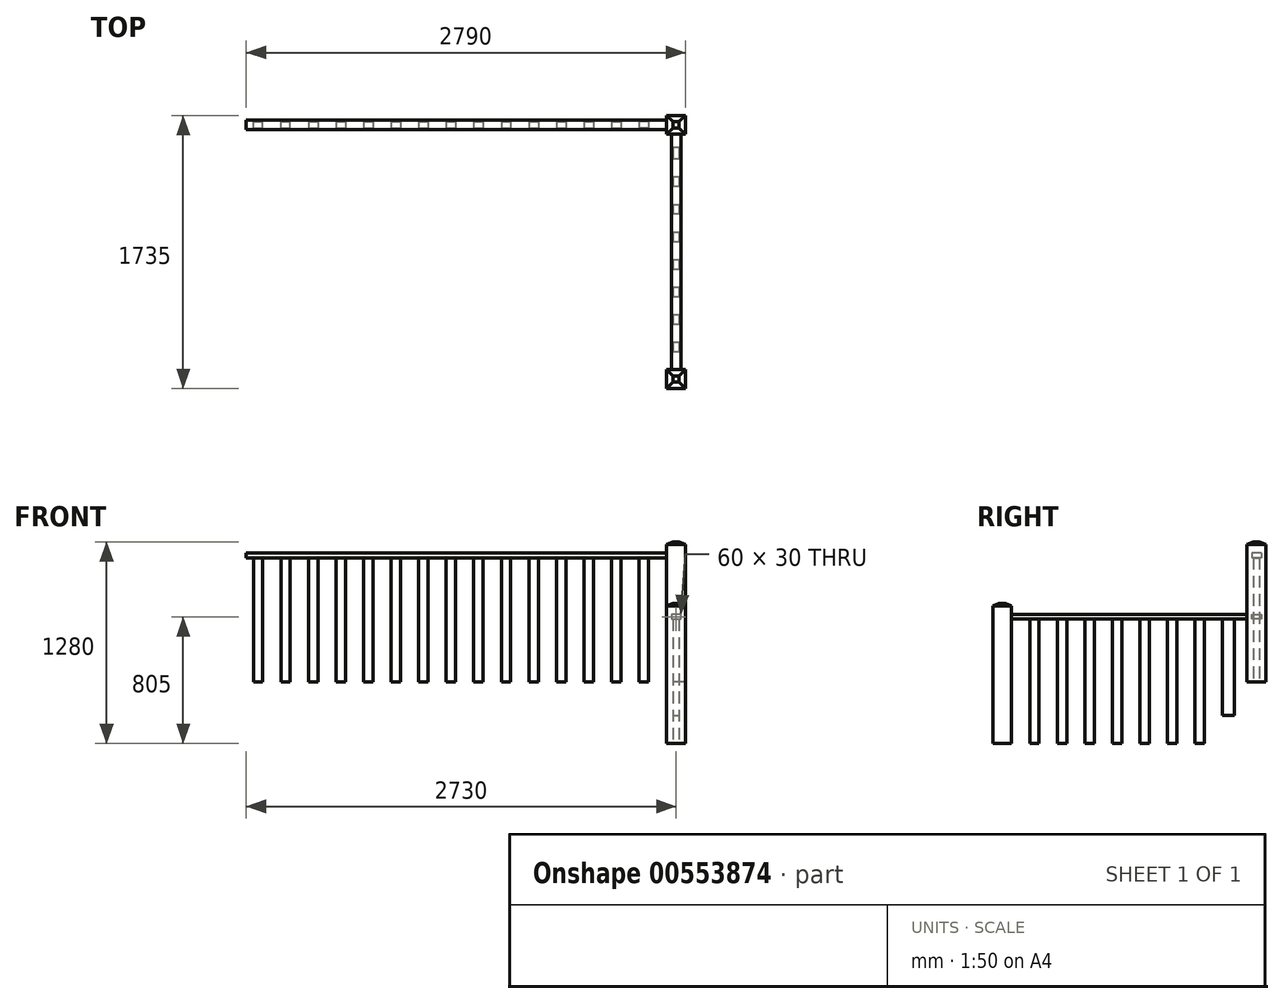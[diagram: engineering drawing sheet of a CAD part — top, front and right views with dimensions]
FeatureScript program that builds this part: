
annotation { "Feature Type Name" : "Feature", "Feature Type Description" : "" }
export const myFeature = defineFeature(function(context is Context, id is Id, definition is map)
    precondition{}
    {
        {
            var Q0;
            Q0=qCreatedBy(makeId("Top.planeOp"),FACE);
            var sketch = newSketch(context, id + "F0", { "sketchPlane" : qUnion([Q0])});
            skLineSegment(sketch, "E0.bottom", {"start": v(-80, 328.24) * mm, "end": v(40, 328.24) * mm});
            skLineSegment(sketch, "E0.top", {"start": v(-80, 208.24) * mm, "end": v(40, 208.24) * mm});
            skLineSegment(sketch, "E0.left", {"start": v(-80, 328.24) * mm, "end": v(-80, 208.24) * mm});
            skLineSegment(sketch, "E0.right", {"start": v(40, 328.24) * mm, "end": v(40, 208.24) * mm});
            skLineSegment(sketch, "E1.top", {"start": v(-80, 1823.24) * mm, "end": v(40, 1823.24) * mm});
            skLineSegment(sketch, "E1.left", {"start": v(-80, 1943.24) * mm, "end": v(-80, 1823.24) * mm});
            skLineSegment(sketch, "E1.right", {"start": v(40, 1943.24) * mm, "end": v(40, 1823.24) * mm});
            skLineSegment(sketch, "E2.bottom", {"start": v(-40, 503.24) * mm, "end": v(0, 503.24) * mm});
            skLineSegment(sketch, "E2.top", {"start": v(-40, 443.24) * mm, "end": v(0, 443.24) * mm});
            skLineSegment(sketch, "E2.left", {"start": v(-40, 503.24) * mm, "end": v(-40, 443.24) * mm});
            skLineSegment(sketch, "E2.right", {"start": v(0, 503.24) * mm, "end": v(0, 443.24) * mm});
            skLineSegment(sketch, "E3.bottom", {"start": v(-40, 678.24) * mm, "end": v(0, 678.24) * mm});
            skLineSegment(sketch, "E3.top", {"start": v(-40, 618.24) * mm, "end": v(0, 618.24) * mm});
            skLineSegment(sketch, "E3.left", {"start": v(-40, 678.24) * mm, "end": v(-40, 618.24) * mm});
            skLineSegment(sketch, "E3.right", {"start": v(0, 678.24) * mm, "end": v(0, 618.24) * mm});
            skLineSegment(sketch, "E4.bottom", {"start": v(-40, 853.24) * mm, "end": v(0, 853.24) * mm});
            skLineSegment(sketch, "E4.top", {"start": v(-40, 793.24) * mm, "end": v(0, 793.24) * mm});
            skLineSegment(sketch, "E4.left", {"start": v(-40, 853.24) * mm, "end": v(-40, 793.24) * mm});
            skLineSegment(sketch, "E4.right", {"start": v(0, 853.24) * mm, "end": v(0, 793.24) * mm});
            skLineSegment(sketch, "E5.bottom", {"start": v(-40, 1028.24) * mm, "end": v(0, 1028.24) * mm});
            skLineSegment(sketch, "E5.top", {"start": v(-40, 968.24) * mm, "end": v(0, 968.24) * mm});
            skLineSegment(sketch, "E5.left", {"start": v(-40, 1028.24) * mm, "end": v(-40, 968.24) * mm});
            skLineSegment(sketch, "E5.right", {"start": v(0, 1028.24) * mm, "end": v(0, 968.24) * mm});
            skLineSegment(sketch, "E6.bottom", {"start": v(-40, 1203.24) * mm, "end": v(0, 1203.24) * mm});
            skLineSegment(sketch, "E6.top", {"start": v(-40, 1143.24) * mm, "end": v(0, 1143.24) * mm});
            skLineSegment(sketch, "E6.left", {"start": v(-40, 1203.24) * mm, "end": v(-40, 1143.24) * mm});
            skLineSegment(sketch, "E6.right", {"start": v(0, 1203.24) * mm, "end": v(0, 1143.24) * mm});
            skLineSegment(sketch, "E7.bottom", {"start": v(-40, 1378.24) * mm, "end": v(0, 1378.24) * mm});
            skLineSegment(sketch, "E7.top", {"start": v(-40, 1318.24) * mm, "end": v(0, 1318.24) * mm});
            skLineSegment(sketch, "E7.left", {"start": v(-40, 1378.24) * mm, "end": v(-40, 1318.24) * mm});
            skLineSegment(sketch, "E7.right", {"start": v(0, 1378.24) * mm, "end": v(0, 1318.24) * mm});
            skLineSegment(sketch, "E8.bottom", {"start": v(-40, 1553.24) * mm, "end": v(0, 1553.24) * mm});
            skLineSegment(sketch, "E8.top", {"start": v(-40, 1493.24) * mm, "end": v(0, 1493.24) * mm});
            skLineSegment(sketch, "E8.left", {"start": v(-40, 1553.24) * mm, "end": v(-40, 1493.24) * mm});
            skLineSegment(sketch, "E8.right", {"start": v(0, 1553.24) * mm, "end": v(0, 1478.21) * mm});
            skLineSegment(sketch, "E9.bottom", {"start": v(-40, 1743.26) * mm, "end": v(0, 1743.26) * mm});
            skLineSegment(sketch, "E9.top", {"start": v(-40, 1668.24) * mm, "end": v(0, 1668.24) * mm});
            skLineSegment(sketch, "E9.left", {"start": v(-40, 1743.26) * mm, "end": v(-40, 1668.24) * mm});
            skLineSegment(sketch, "E9.right", {"start": v(0, 1743.26) * mm, "end": v(0, 1668.24) * mm});
            skLineSegment(sketch, "E10", {"start": v(40, 1943.24) * mm, "end": v(-80, 1943.24) * mm});
            skLineSegment(sketch, "E11.bottom", {"start": v(-195, 1903.24) * mm, "end": v(-255, 1903.24) * mm});
            skLineSegment(sketch, "E11.top", {"start": v(-195, 1863.24) * mm, "end": v(-255, 1863.24) * mm});
            skLineSegment(sketch, "E11.left", {"start": v(-195, 1903.24) * mm, "end": v(-195, 1863.24) * mm});
            skLineSegment(sketch, "E11.right", {"start": v(-255, 1903.24) * mm, "end": v(-255, 1863.24) * mm});
            skLineSegment(sketch, "E12.bottom", {"start": v(-370, 1903.24) * mm, "end": v(-430, 1903.24) * mm});
            skLineSegment(sketch, "E12.top", {"start": v(-370, 1863.24) * mm, "end": v(-430, 1863.24) * mm});
            skLineSegment(sketch, "E12.left", {"start": v(-370, 1903.24) * mm, "end": v(-370, 1863.24) * mm});
            skLineSegment(sketch, "E12.right", {"start": v(-430, 1903.24) * mm, "end": v(-430, 1863.24) * mm});
            skLineSegment(sketch, "E13.bottom", {"start": v(-545, 1903.24) * mm, "end": v(-605, 1903.24) * mm});
            skLineSegment(sketch, "E13.top", {"start": v(-545, 1863.24) * mm, "end": v(-605, 1863.24) * mm});
            skLineSegment(sketch, "E13.left", {"start": v(-545, 1903.24) * mm, "end": v(-545, 1863.24) * mm});
            skLineSegment(sketch, "E13.right", {"start": v(-605, 1903.24) * mm, "end": v(-605, 1863.24) * mm});
            skLineSegment(sketch, "E14.bottom", {"start": v(-720, 1903.24) * mm, "end": v(-780, 1903.24) * mm});
            skLineSegment(sketch, "E14.top", {"start": v(-720, 1863.24) * mm, "end": v(-780, 1863.24) * mm});
            skLineSegment(sketch, "E14.left", {"start": v(-720, 1903.24) * mm, "end": v(-720, 1863.24) * mm});
            skLineSegment(sketch, "E14.right", {"start": v(-780, 1903.24) * mm, "end": v(-780, 1863.24) * mm});
            skLineSegment(sketch, "E15.bottom", {"start": v(-895, 1903.24) * mm, "end": v(-955, 1903.24) * mm});
            skLineSegment(sketch, "E15.top", {"start": v(-895, 1863.24) * mm, "end": v(-955, 1863.24) * mm});
            skLineSegment(sketch, "E15.left", {"start": v(-895, 1903.24) * mm, "end": v(-895, 1863.24) * mm});
            skLineSegment(sketch, "E15.right", {"start": v(-955, 1903.24) * mm, "end": v(-955, 1863.24) * mm});
            skLineSegment(sketch, "E16.bottom", {"start": v(-1070, 1903.24) * mm, "end": v(-1130, 1903.24) * mm});
            skLineSegment(sketch, "E16.top", {"start": v(-1070, 1863.24) * mm, "end": v(-1130, 1863.24) * mm});
            skLineSegment(sketch, "E16.left", {"start": v(-1070, 1903.24) * mm, "end": v(-1070, 1863.24) * mm});
            skLineSegment(sketch, "E16.right", {"start": v(-1130, 1903.24) * mm, "end": v(-1130, 1863.24) * mm});
            skLineSegment(sketch, "E17.bottom", {"start": v(-1245, 1903.24) * mm, "end": v(-1305, 1903.24) * mm});
            skLineSegment(sketch, "E17.top", {"start": v(-1245, 1863.24) * mm, "end": v(-1305, 1863.24) * mm});
            skLineSegment(sketch, "E17.left", {"start": v(-1245, 1903.24) * mm, "end": v(-1245, 1863.24) * mm});
            skLineSegment(sketch, "E17.right", {"start": v(-1305, 1903.24) * mm, "end": v(-1305, 1863.24) * mm});
            skLineSegment(sketch, "E18.bottom", {"start": v(-1420, 1903.24) * mm, "end": v(-1480, 1903.24) * mm});
            skLineSegment(sketch, "E18.top", {"start": v(-1420, 1863.24) * mm, "end": v(-1480, 1863.24) * mm});
            skLineSegment(sketch, "E18.left", {"start": v(-1420, 1903.24) * mm, "end": v(-1420, 1863.24) * mm});
            skLineSegment(sketch, "E18.right", {"start": v(-1480, 1903.24) * mm, "end": v(-1480, 1863.24) * mm});
            skLineSegment(sketch, "E19.bottom", {"start": v(-1655, 1903.24) * mm, "end": v(-1595, 1903.24) * mm});
            skLineSegment(sketch, "E19.top", {"start": v(-1655, 1863.24) * mm, "end": v(-1595, 1863.24) * mm});
            skLineSegment(sketch, "E19.left", {"start": v(-1655, 1903.24) * mm, "end": v(-1655, 1863.24) * mm});
            skLineSegment(sketch, "E19.right", {"start": v(-1595, 1903.24) * mm, "end": v(-1595, 1863.24) * mm});
            skLineSegment(sketch, "E20.bottom", {"start": v(-1830, 1903.24) * mm, "end": v(-1770, 1903.24) * mm});
            skLineSegment(sketch, "E20.top", {"start": v(-1830, 1863.24) * mm, "end": v(-1770, 1863.24) * mm});
            skLineSegment(sketch, "E20.left", {"start": v(-1830, 1903.24) * mm, "end": v(-1830, 1863.24) * mm});
            skLineSegment(sketch, "E20.right", {"start": v(-1770, 1903.24) * mm, "end": v(-1770, 1863.24) * mm});
            skLineSegment(sketch, "E21.bottom", {"start": v(-2005, 1903.24) * mm, "end": v(-1945, 1903.24) * mm});
            skLineSegment(sketch, "E21.top", {"start": v(-2005, 1863.24) * mm, "end": v(-1945, 1863.24) * mm});
            skLineSegment(sketch, "E21.left", {"start": v(-2005, 1903.24) * mm, "end": v(-2005, 1863.24) * mm});
            skLineSegment(sketch, "E21.right", {"start": v(-1945, 1903.24) * mm, "end": v(-1945, 1863.24) * mm});
            skLineSegment(sketch, "E22.bottom", {"start": v(-2180, 1903.24) * mm, "end": v(-2120, 1903.24) * mm});
            skLineSegment(sketch, "E22.top", {"start": v(-2180, 1863.24) * mm, "end": v(-2120, 1863.24) * mm});
            skLineSegment(sketch, "E22.left", {"start": v(-2180, 1903.24) * mm, "end": v(-2180, 1863.24) * mm});
            skLineSegment(sketch, "E22.right", {"start": v(-2120, 1903.24) * mm, "end": v(-2120, 1863.24) * mm});
            skLineSegment(sketch, "E23.bottom", {"start": v(-2355, 1903.24) * mm, "end": v(-2295, 1903.24) * mm});
            skLineSegment(sketch, "E23.top", {"start": v(-2355, 1863.24) * mm, "end": v(-2295, 1863.24) * mm});
            skLineSegment(sketch, "E23.left", {"start": v(-2355, 1903.24) * mm, "end": v(-2355, 1863.24) * mm});
            skLineSegment(sketch, "E23.right", {"start": v(-2295, 1903.24) * mm, "end": v(-2295, 1863.24) * mm});
            skSolve(sketch);
        }
        {
            var Q0;
            Q0=makeQuery(id+"F0.imprint","IMPRINT",FACE,{"disambiguationData":[TD([[makeQuery(id+"F0.imprint","IMPRINT",EDGE,{"derivedFrom":sQuery(id+"F0.wireOp",EDGE,"E23.bottom")}),-1.0]])]});
            var Q1;
            Q1=makeQuery(id+"F0.imprint","IMPRINT",FACE,{"disambiguationData":[TD([[makeQuery(id+"F0.imprint","IMPRINT",EDGE,{"derivedFrom":sQuery(id+"F0.wireOp",EDGE,"E22.bottom")}),-1.0]])]});
            var Q2;
            Q2=makeQuery(id+"F0.imprint","IMPRINT",FACE,{"disambiguationData":[TD([[makeQuery(id+"F0.imprint","IMPRINT",EDGE,{"derivedFrom":sQuery(id+"F0.wireOp",EDGE,"E21.bottom")}),-1.0]])]});
            var Q3;
            Q3=makeQuery(id+"F0.imprint","IMPRINT",FACE,{"disambiguationData":[TD([[makeQuery(id+"F0.imprint","IMPRINT",EDGE,{"derivedFrom":sQuery(id+"F0.wireOp",EDGE,"E20.bottom")}),-1.0]])]});
            var Q4;
            Q4=makeQuery(id+"F0.imprint","IMPRINT",FACE,{"disambiguationData":[TD([[makeQuery(id+"F0.imprint","IMPRINT",EDGE,{"derivedFrom":sQuery(id+"F0.wireOp",EDGE,"E19.bottom")}),-1.0]])]});
            var Q5;
            Q5=makeQuery(id+"F0.imprint","IMPRINT",FACE,{"disambiguationData":[TD([[makeQuery(id+"F0.imprint","IMPRINT",EDGE,{"derivedFrom":sQuery(id+"F0.wireOp",EDGE,"E18.bottom")}),1.0]])]});
            var Q6;
            Q6=makeQuery(id+"F0.imprint","IMPRINT",FACE,{"disambiguationData":[TD([[makeQuery(id+"F0.imprint","IMPRINT",EDGE,{"derivedFrom":sQuery(id+"F0.wireOp",EDGE,"E17.bottom")}),1.0]])]});
            var Q7;
            Q7=makeQuery(id+"F0.imprint","IMPRINT",FACE,{"disambiguationData":[TD([[makeQuery(id+"F0.imprint","IMPRINT",EDGE,{"derivedFrom":sQuery(id+"F0.wireOp",EDGE,"E16.bottom")}),1.0]])]});
            var Q8;
            Q8=makeQuery(id+"F0.imprint","IMPRINT",FACE,{"disambiguationData":[TD([[makeQuery(id+"F0.imprint","IMPRINT",EDGE,{"derivedFrom":sQuery(id+"F0.wireOp",EDGE,"E15.bottom")}),1.0]])]});
            var Q9;
            Q9=makeQuery(id+"F0.imprint","IMPRINT",FACE,{"disambiguationData":[TD([[makeQuery(id+"F0.imprint","IMPRINT",EDGE,{"derivedFrom":sQuery(id+"F0.wireOp",EDGE,"E14.bottom")}),1.0]])]});
            var Q10;
            Q10=makeQuery(id+"F0.imprint","IMPRINT",FACE,{"disambiguationData":[TD([[makeQuery(id+"F0.imprint","IMPRINT",EDGE,{"derivedFrom":sQuery(id+"F0.wireOp",EDGE,"E13.bottom")}),1.0]])]});
            var Q11;
            Q11=makeQuery(id+"F0.imprint","IMPRINT",FACE,{"disambiguationData":[TD([[makeQuery(id+"F0.imprint","IMPRINT",EDGE,{"derivedFrom":sQuery(id+"F0.wireOp",EDGE,"E12.bottom")}),1.0]])]});
            var Q12;
            Q12=makeQuery(id+"F0.imprint","IMPRINT",FACE,{"disambiguationData":[TD([[makeQuery(id+"F0.imprint","IMPRINT",EDGE,{"derivedFrom":sQuery(id+"F0.wireOp",EDGE,"E11.bottom")}),1.0]])]});
            var Q13;
            Q13=makeQuery(id+"F0.imprint","IMPRINT",FACE,{"disambiguationData":[TD([[makeQuery(id+"F0.imprint","IMPRINT",EDGE,{"derivedFrom":sQuery(id+"F0.wireOp",EDGE,"E9.bottom")}),-1.0]])]});
            var Q14;
            {var subQ0=sQuery(id+"F0.wireOp",EDGE,"E8.bottom");Q14=makeQuery(id+"F0.imprint","IMPRINT",FACE,{"disambiguationData":[TD([[makeQuery(id+"F0.imprint","IMPRINT",EDGE,{"derivedFrom":subQ0}),-1.0]])]});}
            var Q15;
            Q15=makeQuery(id+"F0.imprint","IMPRINT",FACE,{"disambiguationData":[TD([[makeQuery(id+"F0.imprint","IMPRINT",EDGE,{"derivedFrom":sQuery(id+"F0.wireOp",EDGE,"E7.bottom")}),-1.0]])]});
            var Q16;
            Q16=makeQuery(id+"F0.imprint","IMPRINT",FACE,{"disambiguationData":[TD([[makeQuery(id+"F0.imprint","IMPRINT",EDGE,{"derivedFrom":sQuery(id+"F0.wireOp",EDGE,"E6.bottom")}),-1.0]])]});
            var Q17;
            Q17=makeQuery(id+"F0.imprint","IMPRINT",FACE,{"disambiguationData":[TD([[makeQuery(id+"F0.imprint","IMPRINT",EDGE,{"derivedFrom":sQuery(id+"F0.wireOp",EDGE,"E5.bottom")}),-1.0]])]});
            var Q18;
            Q18=makeQuery(id+"F0.imprint","IMPRINT",FACE,{"disambiguationData":[TD([[makeQuery(id+"F0.imprint","IMPRINT",EDGE,{"derivedFrom":sQuery(id+"F0.wireOp",EDGE,"E4.bottom")}),-1.0]])]});
            var Q19;
            Q19=makeQuery(id+"F0.imprint","IMPRINT",FACE,{"disambiguationData":[TD([[makeQuery(id+"F0.imprint","IMPRINT",EDGE,{"derivedFrom":sQuery(id+"F0.wireOp",EDGE,"E3.bottom")}),-1.0]])]});
            var Q20;
            Q20=makeQuery(id+"F0.imprint","IMPRINT",FACE,{"disambiguationData":[TD([[makeQuery(id+"F0.imprint","IMPRINT",EDGE,{"derivedFrom":sQuery(id+"F0.wireOp",EDGE,"E2.bottom")}),-1.0]])]});
            var Q21;
            Q21=makeQuery(id+"F0.imprint","IMPRINT",FACE,{"disambiguationData":[TD([[makeQuery(id+"F0.imprint","IMPRINT",EDGE,{"derivedFrom":sQuery(id+"F0.wireOp",EDGE,"E1.top")}),1.0]])]});
            var Q22;
            Q22=makeQuery(id+"F0.imprint","IMPRINT",FACE,{"disambiguationData":[TD([[makeQuery(id+"F0.imprint","IMPRINT",EDGE,{"derivedFrom":sQuery(id+"F0.wireOp",EDGE,"E0.bottom")}),-1.0]])]});
            extrude(context, id + "F1", {"entities" : qUnion([Q0, Q1, Q2, Q3, Q4, Q5, Q6, Q7, Q8, Q9, Q10, Q11, Q12, Q13, Q14, Q15, Q16, Q17, Q18, Q19, Q20, Q21, Q22]), "depth" : 790 * mm});
        }
        {
            var Q0;
            Q0=makeQuery(id+"F1.opExtrude","CAP_FACE",FACE,{"disambiguationData":[OSD([sQuery(id+"F0.wireOp",EDGE,"E9.bottom"),sQuery(id+"F0.wireOp",EDGE,"E9.top"),sQuery(id+"F0.wireOp",EDGE,"E9.left"),sQuery(id+"F0.wireOp",EDGE,"E9.right")])],"isStart":false});
            var sketch = newSketch(context, id + "F2", { "sketchPlane" : qUnion([Q0])});
            skPoint(sketch, "E24.0", {"position": v(-20, 328.24) * mm});
            skLineSegment(sketch, "E25.0", {"start": v(-80, 328.24) * mm, "end": v(40, 328.24) * mm});
            skLineSegment(sketch, "E26.0.0", {"start": v(-80, 328.24) * mm, "end": v(-80, 208.24) * mm});
            skLineSegment(sketch, "E26.0.1", {"start": v(-80, 208.24) * mm, "end": v(40, 208.24) * mm});
            skLineSegment(sketch, "E26.0.2", {"start": v(40, 208.24) * mm, "end": v(40, 328.24) * mm});
            skLineSegment(sketch, "E26.0.3", {"start": v(40, 328.24) * mm, "end": v(-80, 328.24) * mm});
            skLineSegment(sketch, "E27", {"start": v(-50, 1853.24) * mm, "end": v(-2417.72, 1853.24) * mm});
            skLineSegment(sketch, "E28", {"start": v(-2417.72, 1853.24) * mm, "end": v(-2417.72, 1913.24) * mm});
            skLineSegment(sketch, "E29", {"start": v(-2417.72, 1913.24) * mm, "end": v(10, 1913.24) * mm});
            skLineSegment(sketch, "E30", {"start": v(10, 1913.24) * mm, "end": v(10, 328.24) * mm});
            skLineSegment(sketch, "E31", {"start": v(10, 328.24) * mm, "end": v(-50, 328.24) * mm});
            skLineSegment(sketch, "E32", {"start": v(-50, 328.24) * mm, "end": v(-50, 1853.24) * mm});
            skSolve(sketch);
        }
        {
            var Q0;
            Q0=qSketchRegion(id+"F2",true);
            extrude(context, id + "F3", {"entities" : qUnion([Q0]), "depth" : 30 * mm});
        }
        {
            var Q0;
            Q0=makeQuery(id+"F1.opExtrude","CAP_FACE",FACE,{"disambiguationData":[OSD([sQuery(id+"F0.wireOp",EDGE,"E1.top"),sQuery(id+"F0.wireOp",EDGE,"E1.left"),sQuery(id+"F0.wireOp",EDGE,"E1.right"),sQuery(id+"F0.wireOp",EDGE,"E10")])],"isStart":false});
            var sketch = newSketch(context, id + "F4", { "sketchPlane" : qUnion([Q0])});
            skLineSegment(sketch, "E33.0", {"start": v(40, 1943.24) * mm, "end": v(-80, 1943.24) * mm});
            skLineSegment(sketch, "E34.0", {"start": v(-80, 1943.24) * mm, "end": v(-80, 1823.24) * mm});
            skLineSegment(sketch, "E35.0", {"start": v(-80, 1823.24) * mm, "end": v(40, 1823.24) * mm});
            skLineSegment(sketch, "E36.0", {"start": v(40, 1943.24) * mm, "end": v(40, 1823.24) * mm});
            skLineSegment(sketch, "E37.0", {"start": v(-80, 328.24) * mm, "end": v(-80, 208.24) * mm});
            skPoint(sketch, "E38.0", {"position": v(40, 208.24) * mm});
            skLineSegment(sketch, "E39.bottom", {"start": v(-80, 328.24) * mm, "end": v(40, 328.24) * mm});
            skLineSegment(sketch, "E39.top", {"start": v(-80, 208.24) * mm, "end": v(40, 208.24) * mm});
            skLineSegment(sketch, "E39.right", {"start": v(40, 328.24) * mm, "end": v(40, 208.24) * mm});
            skLineSegment(sketch, "E40.bottom", {"start": v(-80, 1943.24) * mm, "end": v(40, 1943.24) * mm});
            skSolve(sketch);
        }
        {
            var Q0;
            Q0=qSketchRegion(id+"F4",true);
            extrude(context, id + "F5", {"entities" : qUnion([Q0]), "depth" : 100 * mm});
        }
        {
            var Q0;
            Q0=makeQuery(id+"F5.opExtrude","CAP_EDGE",EDGE,{"disambiguationData":[OSD([sQuery(id+"F4.wireOp",EDGE,"E39.right")])],"isStart":false});
            var Q1;
            Q1=makeQuery(id+"F5.opExtrude","CAP_EDGE",EDGE,{"disambiguationData":[OSD([sQuery(id+"F4.wireOp",EDGE,"E39.top")])],"isStart":false});
            var Q2;
            Q2=makeQuery(id+"F5.opExtrude","CAP_EDGE",EDGE,{"disambiguationData":[OSD([sQuery(id+"F4.wireOp",EDGE,"E37.0")])],"isStart":false});
            var Q3;
            Q3=makeQuery(id+"F5.opExtrude","CAP_EDGE",EDGE,{"disambiguationData":[OSD([sQuery(id+"F4.wireOp",EDGE,"E39.bottom")])],"isStart":false});
            chamfer(context, id + "F6", {"entities" : qUnion([Q0, Q1, Q2, Q3]), "chamferType" : ChamferType.TWO_OFFSETS, "width1" : 15 * mm, "oppositeDirection" : false, "width2" : 40 * mm, "tangentPropagation" : true});
        }
        {
            var Q0;
            Q0=makeQuery(id+"F1.opExtrude","SWEPT_BODY",BODY,{"disambiguationData":[OSD([sQuery(id+"F0.wireOp",EDGE,"E0.bottom"),sQuery(id+"F0.wireOp",EDGE,"E0.top"),sQuery(id+"F0.wireOp",EDGE,"E0.left"),sQuery(id+"F0.wireOp",EDGE,"E0.right")])]});
            var Q1;
            Q1=makeQuery(id+"F1.opExtrude","SWEPT_BODY",BODY,{"disambiguationData":[OSD([sQuery(id+"F0.wireOp",EDGE,"E1.top"),sQuery(id+"F0.wireOp",EDGE,"E1.left"),sQuery(id+"F0.wireOp",EDGE,"E1.right"),sQuery(id+"F0.wireOp",EDGE,"E10")])]});
            var Q2;
            Q2=makeQuery(id+"F1.opExtrude","SWEPT_BODY",BODY,{"disambiguationData":[OSD([sQuery(id+"F0.wireOp",EDGE,"E2.bottom"),sQuery(id+"F0.wireOp",EDGE,"E2.top"),sQuery(id+"F0.wireOp",EDGE,"E2.left"),sQuery(id+"F0.wireOp",EDGE,"E2.right")])]});
            var Q3;
            Q3=makeQuery(id+"F1.opExtrude","SWEPT_BODY",BODY,{"disambiguationData":[OSD([sQuery(id+"F0.wireOp",EDGE,"E3.bottom"),sQuery(id+"F0.wireOp",EDGE,"E3.top"),sQuery(id+"F0.wireOp",EDGE,"E3.left"),sQuery(id+"F0.wireOp",EDGE,"E3.right")])]});
            var Q4;
            Q4=makeQuery(id+"F1.opExtrude","SWEPT_BODY",BODY,{"disambiguationData":[OSD([sQuery(id+"F0.wireOp",EDGE,"E4.bottom"),sQuery(id+"F0.wireOp",EDGE,"E4.top"),sQuery(id+"F0.wireOp",EDGE,"E4.left"),sQuery(id+"F0.wireOp",EDGE,"E4.right")])]});
            var Q5;
            Q5=makeQuery(id+"F1.opExtrude","SWEPT_BODY",BODY,{"disambiguationData":[OSD([sQuery(id+"F0.wireOp",EDGE,"E5.bottom"),sQuery(id+"F0.wireOp",EDGE,"E5.top"),sQuery(id+"F0.wireOp",EDGE,"E5.left"),sQuery(id+"F0.wireOp",EDGE,"E5.right")])]});
            var Q6;
            Q6=makeQuery(id+"F1.opExtrude","SWEPT_BODY",BODY,{"disambiguationData":[OSD([sQuery(id+"F0.wireOp",EDGE,"E6.bottom"),sQuery(id+"F0.wireOp",EDGE,"E6.top"),sQuery(id+"F0.wireOp",EDGE,"E6.left"),sQuery(id+"F0.wireOp",EDGE,"E6.right")])]});
            var Q7;
            Q7=makeQuery(id+"F1.opExtrude","SWEPT_BODY",BODY,{"disambiguationData":[OSD([sQuery(id+"F0.wireOp",EDGE,"E7.bottom"),sQuery(id+"F0.wireOp",EDGE,"E7.top"),sQuery(id+"F0.wireOp",EDGE,"E7.left"),sQuery(id+"F0.wireOp",EDGE,"E7.right")])]});
            var Q8;
            Q8=makeQuery(id+"F1.opExtrude","SWEPT_BODY",BODY,{"disambiguationData":[OSD([sQuery(id+"F0.wireOp",EDGE,"E8.bottom"),sQuery(id+"F0.wireOp",EDGE,"E8.top"),sQuery(id+"F0.wireOp",EDGE,"E8.left"),sQuery(id+"F0.wireOp",EDGE,"E8.right")])]});
            var Q9;
            Q9=makeQuery(id+"F1.opExtrude","SWEPT_BODY",BODY,{"disambiguationData":[OSD([sQuery(id+"F0.wireOp",EDGE,"E9.bottom"),sQuery(id+"F0.wireOp",EDGE,"E9.top"),sQuery(id+"F0.wireOp",EDGE,"E9.left"),sQuery(id+"F0.wireOp",EDGE,"E9.right")])]});
            var Q10;
            Q10=makeQuery(id+"F1.opExtrude","SWEPT_BODY",BODY,{"disambiguationData":[OSD([sQuery(id+"F0.wireOp",EDGE,"E11.bottom"),sQuery(id+"F0.wireOp",EDGE,"E11.top"),sQuery(id+"F0.wireOp",EDGE,"E11.left"),sQuery(id+"F0.wireOp",EDGE,"E11.right")])]});
            var Q11;
            Q11=makeQuery(id+"F1.opExtrude","SWEPT_BODY",BODY,{"disambiguationData":[OSD([sQuery(id+"F0.wireOp",EDGE,"E12.bottom"),sQuery(id+"F0.wireOp",EDGE,"E12.top"),sQuery(id+"F0.wireOp",EDGE,"E12.left"),sQuery(id+"F0.wireOp",EDGE,"E12.right")])]});
            var Q12;
            Q12=makeQuery(id+"F1.opExtrude","SWEPT_BODY",BODY,{"disambiguationData":[OSD([sQuery(id+"F0.wireOp",EDGE,"E13.bottom"),sQuery(id+"F0.wireOp",EDGE,"E13.top"),sQuery(id+"F0.wireOp",EDGE,"E13.left"),sQuery(id+"F0.wireOp",EDGE,"E13.right")])]});
            var Q13;
            Q13=makeQuery(id+"F1.opExtrude","SWEPT_BODY",BODY,{"disambiguationData":[OSD([sQuery(id+"F0.wireOp",EDGE,"E14.bottom"),sQuery(id+"F0.wireOp",EDGE,"E14.top"),sQuery(id+"F0.wireOp",EDGE,"E14.left"),sQuery(id+"F0.wireOp",EDGE,"E14.right")])]});
            var Q14;
            Q14=makeQuery(id+"F1.opExtrude","SWEPT_BODY",BODY,{"disambiguationData":[OSD([sQuery(id+"F0.wireOp",EDGE,"E15.bottom"),sQuery(id+"F0.wireOp",EDGE,"E15.top"),sQuery(id+"F0.wireOp",EDGE,"E15.left"),sQuery(id+"F0.wireOp",EDGE,"E15.right")])]});
            var Q15;
            Q15=makeQuery(id+"F1.opExtrude","SWEPT_BODY",BODY,{"disambiguationData":[OSD([sQuery(id+"F0.wireOp",EDGE,"E16.bottom"),sQuery(id+"F0.wireOp",EDGE,"E16.top"),sQuery(id+"F0.wireOp",EDGE,"E16.left"),sQuery(id+"F0.wireOp",EDGE,"E16.right")])]});
            var Q16;
            Q16=makeQuery(id+"F1.opExtrude","SWEPT_BODY",BODY,{"disambiguationData":[OSD([sQuery(id+"F0.wireOp",EDGE,"E17.bottom"),sQuery(id+"F0.wireOp",EDGE,"E17.top"),sQuery(id+"F0.wireOp",EDGE,"E17.left"),sQuery(id+"F0.wireOp",EDGE,"E17.right")])]});
            var Q17;
            Q17=makeQuery(id+"F1.opExtrude","SWEPT_BODY",BODY,{"disambiguationData":[OSD([sQuery(id+"F0.wireOp",EDGE,"E18.bottom"),sQuery(id+"F0.wireOp",EDGE,"E18.top"),sQuery(id+"F0.wireOp",EDGE,"E18.left"),sQuery(id+"F0.wireOp",EDGE,"E18.right")])]});
            var Q18;
            Q18=makeQuery(id+"F1.opExtrude","SWEPT_BODY",BODY,{"disambiguationData":[OSD([sQuery(id+"F0.wireOp",EDGE,"E19.bottom"),sQuery(id+"F0.wireOp",EDGE,"E19.top"),sQuery(id+"F0.wireOp",EDGE,"E19.left"),sQuery(id+"F0.wireOp",EDGE,"E19.right")])]});
            var Q19;
            Q19=makeQuery(id+"F1.opExtrude","SWEPT_BODY",BODY,{"disambiguationData":[OSD([sQuery(id+"F0.wireOp",EDGE,"E20.bottom"),sQuery(id+"F0.wireOp",EDGE,"E20.top"),sQuery(id+"F0.wireOp",EDGE,"E20.left"),sQuery(id+"F0.wireOp",EDGE,"E20.right")])]});
            var Q20;
            Q20=makeQuery(id+"F1.opExtrude","SWEPT_BODY",BODY,{"disambiguationData":[OSD([sQuery(id+"F0.wireOp",EDGE,"E21.bottom"),sQuery(id+"F0.wireOp",EDGE,"E21.top"),sQuery(id+"F0.wireOp",EDGE,"E21.left"),sQuery(id+"F0.wireOp",EDGE,"E21.right")])]});
            var Q21;
            Q21=makeQuery(id+"F1.opExtrude","SWEPT_BODY",BODY,{"disambiguationData":[OSD([sQuery(id+"F0.wireOp",EDGE,"E22.bottom"),sQuery(id+"F0.wireOp",EDGE,"E22.top"),sQuery(id+"F0.wireOp",EDGE,"E22.left"),sQuery(id+"F0.wireOp",EDGE,"E22.right")])]});
            var Q22;
            Q22=makeQuery(id+"F1.opExtrude","SWEPT_BODY",BODY,{"disambiguationData":[OSD([sQuery(id+"F0.wireOp",EDGE,"E23.bottom"),sQuery(id+"F0.wireOp",EDGE,"E23.top"),sQuery(id+"F0.wireOp",EDGE,"E23.left"),sQuery(id+"F0.wireOp",EDGE,"E23.right")])]});
            var Q23;
            Q23=makeQuery(id+"F3.opExtrude","SWEPT_BODY",BODY,{"disambiguationData":[OSD([sQuery(id+"F2.wireOp",EDGE,"E26.0.0"),sQuery(id+"F2.wireOp",EDGE,"E26.0.1"),sQuery(id+"F2.wireOp",EDGE,"E26.0.2"),sQuery(id+"F2.wireOp",EDGE,"E26.0.3"),sQuery(id+"F2.wireOp",EDGE,"E27"),sQuery(id+"F2.wireOp",EDGE,"E28"),sQuery(id+"F2.wireOp",EDGE,"E29"),sQuery(id+"F2.wireOp",EDGE,"E30"),sQuery(id+"F2.wireOp",EDGE,"E32")])]});
            var Q24;
            Q24=makeQuery(id+"F5.opExtrude","SWEPT_BODY",BODY,{"disambiguationData":[OSD([sQuery(id+"F4.wireOp",EDGE,"E39.bottom"),sQuery(id+"F4.wireOp",EDGE,"E39.top"),sQuery(id+"F4.wireOp",EDGE,"E37.0"),sQuery(id+"F4.wireOp",EDGE,"E39.right")])]});
            var Q25;
            Q25=makeQuery(id+"F5.opExtrude","SWEPT_BODY",BODY,{"disambiguationData":[OSD([sQuery(id+"F4.wireOp",EDGE,"E40.bottom"),sQuery(id+"F4.wireOp",EDGE,"E35.0"),sQuery(id+"F4.wireOp",EDGE,"E34.0"),sQuery(id+"F4.wireOp",EDGE,"E36.0")])]});
            booleanBodies(context, id + "F7", {"operationType" : BooleanOperationType.UNION, "tools" : qUnion([Q0, Q1, Q2, Q3, Q4, Q5, Q6, Q7, Q8, Q9, Q10, Q11, Q12, Q13, Q14, Q15, Q16, Q17, Q18, Q19, Q20, Q21, Q22, Q23, Q24, Q25])});
        }
        {
            var Q0;
            Q0=makeQuery(id+"F1.opExtrude","CAP_FACE",FACE,{"disambiguationData":[OSD([sQuery(id+"F0.wireOp",EDGE,"E23.bottom"),sQuery(id+"F0.wireOp",EDGE,"E23.top"),sQuery(id+"F0.wireOp",EDGE,"E23.left"),sQuery(id+"F0.wireOp",EDGE,"E23.right")])],"isStart":true});
            var sketch = newSketch(context, id + "F8", { "sketchPlane" : qUnion([Q0])});
            skLineSegment(sketch, "E41.top", {"start": v(-2551.9, -1788.92) * mm, "end": v(302.39, -1788.92) * mm});
            skLineSegment(sketch, "E41.left", {"start": v(-2551.9, -1948.92) * mm, "end": v(-2551.9, -1788.92) * mm});
            skLineSegment(sketch, "E41.right", {"start": v(302.39, -1948.92) * mm, "end": v(302.39, -1788.92) * mm});
            skLineSegment(sketch, "E42", {"start": v(-2551.9, -1948.92) * mm, "end": v(302.39, -1948.92) * mm});
            skSolve(sketch);
        }
        {
            var Q0;
            Q0=makeQuery(id+"F8.imprint","IMPRINT",FACE,{"disambiguationData":[TD([[makeQuery(id+"F8.imprint","IMPRINT",EDGE,{"derivedFrom":sQuery(id+"F8.wireOp",EDGE,"E41.top")}),-1.0]])]});
            var Q1;
            Q1=makeQuery(id+"F8.imprint","IMPRINT",FACE,{"disambiguationData":[TD([[makeQuery(id+"F8.imprint","IMPRINT",EDGE,{"derivedFrom":makeQuery(id+"F1.opExtrude","CAP_EDGE",EDGE,{"disambiguationData":[OSD([sQuery(id+"F0.wireOp",EDGE,"E23.bottom")])],"isStart":true})}),1.0]])]});
            extrude(context, id + "F9", {"entities" : qUnion([Q0, Q1]), "operationType" : NewBodyOperationType.REMOVE, "oppositeDirection" : true, "depth" : 390 * mm});
        }
        {
            var Q0;
            Q0=makeQuery(id+"F1.opExtrude","CAP_FACE",FACE,{"disambiguationData":[OSD([sQuery(id+"F0.wireOp",EDGE,"E9.bottom"),sQuery(id+"F0.wireOp",EDGE,"E9.top"),sQuery(id+"F0.wireOp",EDGE,"E9.left"),sQuery(id+"F0.wireOp",EDGE,"E9.right")])],"isStart":true});
            var sketch = newSketch(context, id + "F10", { "sketchPlane" : qUnion([Q0])});
            skSolve(sketch);
        }
        {
            var Q0;
            Q0=makeQuery(id+"F10.imprint","IMPRINT",FACE,{"disambiguationData":[TD([[makeQuery(id+"F10.imprint","IMPRINT",EDGE,{"derivedFrom":makeQuery(id+"F1.opExtrude","CAP_EDGE",EDGE,{"disambiguationData":[OSD([sQuery(id+"F0.wireOp",EDGE,"E9.bottom")])],"isStart":true})}),1.0]])]});
            extrude(context, id + "F11", {"entities" : qUnion([Q0]), "operationType" : NewBodyOperationType.REMOVE, "oppositeDirection" : true, "depth" : 180 * mm});
        }
        {
            var Q0;
            Q0=makeQuery(id+"F5.opExtrude","CAP_FACE",FACE,{"disambiguationData":[OSD([sQuery(id+"F4.wireOp",EDGE,"E40.bottom"),sQuery(id+"F4.wireOp",EDGE,"E35.0"),sQuery(id+"F4.wireOp",EDGE,"E34.0"),sQuery(id+"F4.wireOp",EDGE,"E36.0")])],"isStart":false});
            var sketch = newSketch(context, id + "F12", { "sketchPlane" : qUnion([Q0])});
            skPoint(sketch, "E43.0", {"position": v(-80, 1943.24) * mm});
            skPoint(sketch, "E44.0", {"position": v(40, 1823.24) * mm});
            skLineSegment(sketch, "E45.bottom", {"start": v(-80, 1943.24) * mm, "end": v(40, 1943.24) * mm});
            skLineSegment(sketch, "E45.top", {"start": v(-80, 1823.24) * mm, "end": v(40, 1823.24) * mm});
            skLineSegment(sketch, "E45.left", {"start": v(-80, 1943.24) * mm, "end": v(-80, 1823.24) * mm});
            skLineSegment(sketch, "E45.right", {"start": v(40, 1943.24) * mm, "end": v(40, 1823.24) * mm});
            skSolve(sketch);
        }
        {
            var Q0;
            Q0=makeQuery(id+"F12.imprint","IMPRINT",FACE,{"disambiguationData":[TD([[makeQuery(id+"F12.imprint","IMPRINT",EDGE,{"derivedFrom":sQuery(id+"F12.wireOp",EDGE,"E45.bottom")}),1.0]])]});
            extrude(context, id + "F13", {"entities" : qUnion([Q0]), "operationType" : NewBodyOperationType.ADD, "depth" : 390 * mm});
        }
        {
            var Q0;
            Q0=makeQuery(id+"F13.opExtrude","CAP_EDGE",EDGE,{"disambiguationData":[OSD([sQuery(id+"F12.wireOp",EDGE,"E45.top")])],"isStart":false});
            var Q1;
            Q1=makeQuery(id+"F13.opExtrude","CAP_EDGE",EDGE,{"disambiguationData":[OSD([sQuery(id+"F12.wireOp",EDGE,"E45.left")])],"isStart":false});
            var Q2;
            Q2=makeQuery(id+"F13.opExtrude","CAP_EDGE",EDGE,{"disambiguationData":[OSD([sQuery(id+"F12.wireOp",EDGE,"E45.bottom")])],"isStart":false});
            var Q3;
            Q3=makeQuery(id+"F13.opExtrude","CAP_EDGE",EDGE,{"disambiguationData":[OSD([sQuery(id+"F12.wireOp",EDGE,"E45.right")])],"isStart":false});
            chamfer(context, id + "F14", {"entities" : qUnion([Q0, Q1, Q2, Q3]), "chamferType" : ChamferType.TWO_OFFSETS, "width1" : 40 * mm, "oppositeDirection" : false, "width2" : 15 * mm, "tangentPropagation" : true});
        }
        {
            var Q0;
            Q0=makeQuery(id+"F3.opExtrude","SWEPT_FACE",FACE,{"disambiguationData":[OSD([sQuery(id+"F2.wireOp",EDGE,"E28")])]});
            var sketch = newSketch(context, id + "F15", { "sketchPlane" : qUnion([Q0])});
            skPoint(sketch, "E46.0", {"position": v(-1913.24, 790) * mm});
            skPoint(sketch, "E47.0", {"position": v(-1853.24, 820) * mm});
            skLineSegment(sketch, "E48.bottom", {"start": v(-1913.24, 790) * mm, "end": v(-1853.24, 790) * mm});
            skLineSegment(sketch, "E48.top", {"start": v(-1913.24, 820) * mm, "end": v(-1853.24, 820) * mm});
            skLineSegment(sketch, "E48.left", {"start": v(-1913.24, 790) * mm, "end": v(-1913.24, 820) * mm});
            skLineSegment(sketch, "E48.right", {"start": v(-1853.24, 790) * mm, "end": v(-1853.24, 820) * mm});
            skSolve(sketch);
        }
        {
            var Q0;
            Q0=makeQuery(id+"F15.imprint","IMPRINT",FACE,{"disambiguationData":[TD([[makeQuery(id+"F15.imprint","IMPRINT",EDGE,{"derivedFrom":sQuery(id+"F15.wireOp",EDGE,"E48.bottom")}),-1.0]])]});
            extrude(context, id + "F16", {"entities" : qUnion([Q0]), "operationType" : NewBodyOperationType.REMOVE, "oppositeDirection" : true, "depth" : 2337.74 * mm});
        }
        {
            var Q0;
            Q0=makeQuery(id+"F16.boolean.opBoolean","COPY",FACE,{"disambiguationData":[TD([makeQuery(id+"F1.opExtrude","SWEPT_FACE",FACE,{"disambiguationData":[OSD([sQuery(id+"F0.wireOp",EDGE,"E11.bottom")])]})])],"derivedFrom":makeQuery(id+"F16.opExtrude","SWEPT_FACE",FACE,{"disambiguationData":[OSD([sQuery(id+"F15.wireOp",EDGE,"E48.bottom")])]})});
            var sketch = newSketch(context, id + "F17", { "sketchPlane" : qUnion([Q0])});
            skPoint(sketch, "E49.0", {"position": v(-2355, 1903.24) * mm});
            skPoint(sketch, "E50.0", {"position": v(-2295, 1863.24) * mm});
            skPoint(sketch, "E51.0", {"position": v(-2180, 1903.24) * mm});
            skPoint(sketch, "E52.0", {"position": v(-2120, 1863.24) * mm});
            skPoint(sketch, "E53.0", {"position": v(-2005, 1903.24) * mm});
            skPoint(sketch, "E54.0", {"position": v(-1945, 1863.24) * mm});
            skPoint(sketch, "E55.0", {"position": v(-1830, 1903.24) * mm});
            skPoint(sketch, "E56.0", {"position": v(-1770, 1863.24) * mm});
            skPoint(sketch, "E57.0", {"position": v(-1655, 1903.24) * mm});
            skPoint(sketch, "E58.0", {"position": v(-1595, 1863.24) * mm});
            skPoint(sketch, "E59.0", {"position": v(-1480, 1903.24) * mm});
            skPoint(sketch, "E60.0", {"position": v(-1420, 1863.24) * mm});
            skPoint(sketch, "E61.0", {"position": v(-1305, 1903.24) * mm});
            skPoint(sketch, "E62.0", {"position": v(-1245, 1863.24) * mm});
            skPoint(sketch, "E63.0", {"position": v(-1130, 1903.24) * mm});
            skPoint(sketch, "E64.0", {"position": v(-1070, 1863.24) * mm});
            skPoint(sketch, "E65.0", {"position": v(-955, 1903.24) * mm});
            skPoint(sketch, "E66.0", {"position": v(-895, 1863.24) * mm});
            skPoint(sketch, "E67.0", {"position": v(-780, 1903.24) * mm});
            skPoint(sketch, "E68.0", {"position": v(-720, 1863.24) * mm});
            skPoint(sketch, "E69.0", {"position": v(-605, 1903.24) * mm});
            skPoint(sketch, "E70.0", {"position": v(-545, 1863.24) * mm});
            skPoint(sketch, "E71.0", {"position": v(-430, 1903.24) * mm});
            skPoint(sketch, "E72.0", {"position": v(-370, 1863.24) * mm});
            skPoint(sketch, "E73.0", {"position": v(-255, 1903.24) * mm});
            skPoint(sketch, "E74.0", {"position": v(-195, 1863.24) * mm});
            skLineSegment(sketch, "E75.bottom", {"start": v(-255, 1903.24) * mm, "end": v(-195, 1903.24) * mm});
            skLineSegment(sketch, "E75.top", {"start": v(-255, 1863.24) * mm, "end": v(-195, 1863.24) * mm});
            skLineSegment(sketch, "E75.left", {"start": v(-255, 1903.24) * mm, "end": v(-255, 1863.24) * mm});
            skLineSegment(sketch, "E75.right", {"start": v(-195, 1903.24) * mm, "end": v(-195, 1863.24) * mm});
            skLineSegment(sketch, "E76.bottom", {"start": v(-430, 1903.24) * mm, "end": v(-370, 1903.24) * mm});
            skLineSegment(sketch, "E76.top", {"start": v(-430, 1863.24) * mm, "end": v(-370, 1863.24) * mm});
            skLineSegment(sketch, "E76.left", {"start": v(-430, 1903.24) * mm, "end": v(-430, 1863.24) * mm});
            skLineSegment(sketch, "E76.right", {"start": v(-370, 1903.24) * mm, "end": v(-370, 1863.24) * mm});
            skLineSegment(sketch, "E77.bottom", {"start": v(-605, 1903.24) * mm, "end": v(-545, 1903.24) * mm});
            skLineSegment(sketch, "E77.top", {"start": v(-605, 1863.24) * mm, "end": v(-545, 1863.24) * mm});
            skLineSegment(sketch, "E77.left", {"start": v(-605, 1903.24) * mm, "end": v(-605, 1863.24) * mm});
            skLineSegment(sketch, "E77.right", {"start": v(-545, 1903.24) * mm, "end": v(-545, 1863.24) * mm});
            skLineSegment(sketch, "E78.bottom", {"start": v(-780, 1903.24) * mm, "end": v(-720, 1903.24) * mm});
            skLineSegment(sketch, "E78.top", {"start": v(-780, 1863.24) * mm, "end": v(-720, 1863.24) * mm});
            skLineSegment(sketch, "E78.left", {"start": v(-780, 1903.24) * mm, "end": v(-780, 1863.24) * mm});
            skLineSegment(sketch, "E78.right", {"start": v(-720, 1903.24) * mm, "end": v(-720, 1863.24) * mm});
            skLineSegment(sketch, "E79.bottom", {"start": v(-955, 1903.24) * mm, "end": v(-895, 1903.24) * mm});
            skLineSegment(sketch, "E79.top", {"start": v(-955, 1863.24) * mm, "end": v(-895, 1863.24) * mm});
            skLineSegment(sketch, "E79.left", {"start": v(-955, 1903.24) * mm, "end": v(-955, 1863.24) * mm});
            skLineSegment(sketch, "E79.right", {"start": v(-895, 1903.24) * mm, "end": v(-895, 1863.24) * mm});
            skLineSegment(sketch, "E80.bottom", {"start": v(-1130, 1903.24) * mm, "end": v(-1070, 1903.24) * mm});
            skLineSegment(sketch, "E80.top", {"start": v(-1130, 1863.24) * mm, "end": v(-1070, 1863.24) * mm});
            skLineSegment(sketch, "E80.left", {"start": v(-1130, 1903.24) * mm, "end": v(-1130, 1863.24) * mm});
            skLineSegment(sketch, "E80.right", {"start": v(-1070, 1903.24) * mm, "end": v(-1070, 1863.24) * mm});
            skLineSegment(sketch, "E81.bottom", {"start": v(-1305, 1903.24) * mm, "end": v(-1245, 1903.24) * mm});
            skLineSegment(sketch, "E81.top", {"start": v(-1305, 1863.24) * mm, "end": v(-1245, 1863.24) * mm});
            skLineSegment(sketch, "E81.left", {"start": v(-1305, 1903.24) * mm, "end": v(-1305, 1863.24) * mm});
            skLineSegment(sketch, "E81.right", {"start": v(-1245, 1903.24) * mm, "end": v(-1245, 1863.24) * mm});
            skLineSegment(sketch, "E82.bottom", {"start": v(-1480, 1903.24) * mm, "end": v(-1420, 1903.24) * mm});
            skLineSegment(sketch, "E82.top", {"start": v(-1480, 1863.24) * mm, "end": v(-1420, 1863.24) * mm});
            skLineSegment(sketch, "E82.left", {"start": v(-1480, 1903.24) * mm, "end": v(-1480, 1863.24) * mm});
            skLineSegment(sketch, "E82.right", {"start": v(-1420, 1903.24) * mm, "end": v(-1420, 1863.24) * mm});
            skLineSegment(sketch, "E83.bottom", {"start": v(-1655, 1903.24) * mm, "end": v(-1595, 1903.24) * mm});
            skLineSegment(sketch, "E83.top", {"start": v(-1655, 1863.24) * mm, "end": v(-1595, 1863.24) * mm});
            skLineSegment(sketch, "E83.left", {"start": v(-1655, 1903.24) * mm, "end": v(-1655, 1863.24) * mm});
            skLineSegment(sketch, "E83.right", {"start": v(-1595, 1903.24) * mm, "end": v(-1595, 1863.24) * mm});
            skLineSegment(sketch, "E84.bottom", {"start": v(-1830, 1903.24) * mm, "end": v(-1770, 1903.24) * mm});
            skLineSegment(sketch, "E84.top", {"start": v(-1830, 1863.24) * mm, "end": v(-1770, 1863.24) * mm});
            skLineSegment(sketch, "E84.left", {"start": v(-1830, 1903.24) * mm, "end": v(-1830, 1863.24) * mm});
            skLineSegment(sketch, "E84.right", {"start": v(-1770, 1903.24) * mm, "end": v(-1770, 1863.24) * mm});
            skLineSegment(sketch, "E85.bottom", {"start": v(-2005, 1903.24) * mm, "end": v(-1945, 1903.24) * mm});
            skLineSegment(sketch, "E85.top", {"start": v(-2005, 1863.24) * mm, "end": v(-1945, 1863.24) * mm});
            skLineSegment(sketch, "E85.left", {"start": v(-2005, 1903.24) * mm, "end": v(-2005, 1863.24) * mm});
            skLineSegment(sketch, "E85.right", {"start": v(-1945, 1903.24) * mm, "end": v(-1945, 1863.24) * mm});
            skLineSegment(sketch, "E86.bottom", {"start": v(-2180, 1903.24) * mm, "end": v(-2120, 1903.24) * mm});
            skLineSegment(sketch, "E86.top", {"start": v(-2180, 1863.24) * mm, "end": v(-2120, 1863.24) * mm});
            skLineSegment(sketch, "E86.left", {"start": v(-2180, 1903.24) * mm, "end": v(-2180, 1863.24) * mm});
            skLineSegment(sketch, "E86.right", {"start": v(-2120, 1903.24) * mm, "end": v(-2120, 1863.24) * mm});
            skLineSegment(sketch, "E87.bottom", {"start": v(-2355, 1903.24) * mm, "end": v(-2295, 1903.24) * mm});
            skLineSegment(sketch, "E87.top", {"start": v(-2355, 1863.24) * mm, "end": v(-2295, 1863.24) * mm});
            skLineSegment(sketch, "E87.left", {"start": v(-2355, 1903.24) * mm, "end": v(-2355, 1863.24) * mm});
            skLineSegment(sketch, "E87.right", {"start": v(-2295, 1903.24) * mm, "end": v(-2295, 1863.24) * mm});
            skSolve(sketch);
        }
        {
            var Q0;
            Q0=makeQuery(id+"F17.imprint","IMPRINT",FACE,{"disambiguationData":[TD([[makeQuery(id+"F17.imprint","IMPRINT",EDGE,{"derivedFrom":sQuery(id+"F17.wireOp",EDGE,"E87.bottom")}),-1.0]])]});
            var Q1;
            Q1=makeQuery(id+"F17.imprint","IMPRINT",FACE,{"disambiguationData":[TD([[makeQuery(id+"F17.imprint","IMPRINT",EDGE,{"derivedFrom":sQuery(id+"F17.wireOp",EDGE,"E86.bottom")}),-1.0]])]});
            var Q2;
            Q2=makeQuery(id+"F17.imprint","IMPRINT",FACE,{"disambiguationData":[TD([[makeQuery(id+"F17.imprint","IMPRINT",EDGE,{"derivedFrom":sQuery(id+"F17.wireOp",EDGE,"E85.bottom")}),-1.0]])]});
            var Q3;
            Q3=makeQuery(id+"F17.imprint","IMPRINT",FACE,{"disambiguationData":[TD([[makeQuery(id+"F17.imprint","IMPRINT",EDGE,{"derivedFrom":sQuery(id+"F17.wireOp",EDGE,"E84.bottom")}),-1.0]])]});
            var Q4;
            Q4=makeQuery(id+"F17.imprint","IMPRINT",FACE,{"disambiguationData":[TD([[makeQuery(id+"F17.imprint","IMPRINT",EDGE,{"derivedFrom":sQuery(id+"F17.wireOp",EDGE,"E83.bottom")}),-1.0]])]});
            var Q5;
            Q5=makeQuery(id+"F17.imprint","IMPRINT",FACE,{"disambiguationData":[TD([[makeQuery(id+"F17.imprint","IMPRINT",EDGE,{"derivedFrom":sQuery(id+"F17.wireOp",EDGE,"E82.bottom")}),-1.0]])]});
            var Q6;
            Q6=makeQuery(id+"F17.imprint","IMPRINT",FACE,{"disambiguationData":[TD([[makeQuery(id+"F17.imprint","IMPRINT",EDGE,{"derivedFrom":sQuery(id+"F17.wireOp",EDGE,"E81.bottom")}),-1.0]])]});
            var Q7;
            Q7=makeQuery(id+"F17.imprint","IMPRINT",FACE,{"disambiguationData":[TD([[makeQuery(id+"F17.imprint","IMPRINT",EDGE,{"derivedFrom":sQuery(id+"F17.wireOp",EDGE,"E80.bottom")}),-1.0]])]});
            var Q8;
            Q8=makeQuery(id+"F17.imprint","IMPRINT",FACE,{"disambiguationData":[TD([[makeQuery(id+"F17.imprint","IMPRINT",EDGE,{"derivedFrom":sQuery(id+"F17.wireOp",EDGE,"E79.bottom")}),-1.0]])]});
            var Q9;
            Q9=makeQuery(id+"F17.imprint","IMPRINT",FACE,{"disambiguationData":[TD([[makeQuery(id+"F17.imprint","IMPRINT",EDGE,{"derivedFrom":sQuery(id+"F17.wireOp",EDGE,"E78.bottom")}),-1.0]])]});
            var Q10;
            Q10=makeQuery(id+"F17.imprint","IMPRINT",FACE,{"disambiguationData":[TD([[makeQuery(id+"F17.imprint","IMPRINT",EDGE,{"derivedFrom":sQuery(id+"F17.wireOp",EDGE,"E77.bottom")}),-1.0]])]});
            var Q11;
            Q11=makeQuery(id+"F17.imprint","IMPRINT",FACE,{"disambiguationData":[TD([[makeQuery(id+"F17.imprint","IMPRINT",EDGE,{"derivedFrom":sQuery(id+"F17.wireOp",EDGE,"E76.bottom")}),-1.0]])]});
            var Q12;
            Q12=makeQuery(id+"F17.imprint","IMPRINT",FACE,{"disambiguationData":[TD([[makeQuery(id+"F17.imprint","IMPRINT",EDGE,{"derivedFrom":sQuery(id+"F17.wireOp",EDGE,"E75.bottom")}),1.0]])]});
            extrude(context, id + "F18", {"entities" : qUnion([Q0, Q1, Q2, Q3, Q4, Q5, Q6, Q7, Q8, Q9, Q10, Q11, Q12]), "operationType" : NewBodyOperationType.ADD, "depth" : 390 * mm});
        }
        {
            var Q0;
            Q0=makeQuery(id+"F13.boolean.opBoolean","MERGE",FACE,{"derivedFrom":[makeQuery(id+"F7.opBoolean","MERGE",FACE,{"derivedFrom":[makeQuery(id+"F1.opExtrude","SWEPT_FACE",FACE,{"disambiguationData":[OSD([sQuery(id+"F0.wireOp",EDGE,"E1.left")])]}),makeQuery(id+"F5.opExtrude","SWEPT_FACE",FACE,{"disambiguationData":[OSD([sQuery(id+"F4.wireOp",EDGE,"E34.0")])]})]}),makeQuery(id+"F13.opExtrude","SWEPT_FACE",FACE,{"disambiguationData":[OSD([sQuery(id+"F12.wireOp",EDGE,"E45.left")])]})]});
            var sketch = newSketch(context, id + "F19", { "sketchPlane" : qUnion([Q0])});
            skLineSegment(sketch, "E88.bottom", {"start": v(-1913.24, 1210) * mm, "end": v(-1853.24, 1210) * mm});
            skLineSegment(sketch, "E88.top", {"start": v(-1913.24, 1180) * mm, "end": v(-1853.24, 1180) * mm});
            skLineSegment(sketch, "E88.left", {"start": v(-1913.24, 1210) * mm, "end": v(-1913.24, 1180) * mm});
            skLineSegment(sketch, "E88.right", {"start": v(-1853.24, 1210) * mm, "end": v(-1853.24, 1180) * mm});
            skSolve(sketch);
        }
        {
            var Q0;
            Q0=makeQuery(id+"F19.imprint","IMPRINT",FACE,{"disambiguationData":[TD([[makeQuery(id+"F19.imprint","IMPRINT",EDGE,{"derivedFrom":sQuery(id+"F19.wireOp",EDGE,"E88.bottom")}),-1.0]])]});
            extrude(context, id + "F20", {"entities" : qUnion([Q0]), "operationType" : NewBodyOperationType.ADD, "depth" : 2670 * mm});
        }
        {
            var Q0;
            Q0=makeQuery(id+"F20.opExtrude","SWEPT_FACE",FACE,{"disambiguationData":[OSD([sQuery(id+"F19.wireOp",EDGE,"E88.top")])]});
            var sketch = newSketch(context, id + "F21", { "sketchPlane" : qUnion([Q0])});
            skLineSegment(sketch, "E89.bottom", {"start": v(-2530, -1863.24) * mm, "end": v(-2470, -1863.24) * mm});
            skLineSegment(sketch, "E89.top", {"start": v(-2530, -1903.24) * mm, "end": v(-2470, -1903.24) * mm});
            skLineSegment(sketch, "E89.left", {"start": v(-2530, -1863.24) * mm, "end": v(-2530, -1903.24) * mm});
            skLineSegment(sketch, "E89.right", {"start": v(-2470, -1863.24) * mm, "end": v(-2470, -1903.24) * mm});
            skLineSegment(sketch, "E90.bottom", {"start": v(-2705, -1863.24) * mm, "end": v(-2645, -1863.24) * mm});
            skLineSegment(sketch, "E90.top", {"start": v(-2705, -1903.24) * mm, "end": v(-2645, -1903.24) * mm});
            skLineSegment(sketch, "E90.left", {"start": v(-2705, -1863.24) * mm, "end": v(-2705, -1903.24) * mm});
            skLineSegment(sketch, "E90.right", {"start": v(-2645, -1863.24) * mm, "end": v(-2645, -1903.24) * mm});
            skSolve(sketch);
        }
        {
            var Q0;
            Q0=makeQuery(id+"F21.imprint","IMPRINT",FACE,{"disambiguationData":[TD([[makeQuery(id+"F21.imprint","IMPRINT",EDGE,{"derivedFrom":sQuery(id+"F21.wireOp",EDGE,"E90.bottom")}),-1.0]])]});
            var Q1;
            Q1=makeQuery(id+"F21.imprint","IMPRINT",FACE,{"disambiguationData":[TD([[makeQuery(id+"F21.imprint","IMPRINT",EDGE,{"derivedFrom":sQuery(id+"F21.wireOp",EDGE,"E89.bottom")}),-1.0]])]});
            extrude(context, id + "F22", {"entities" : qUnion([Q0, Q1]), "operationType" : NewBodyOperationType.ADD, "depth" : 790 * mm});
        }
    });
